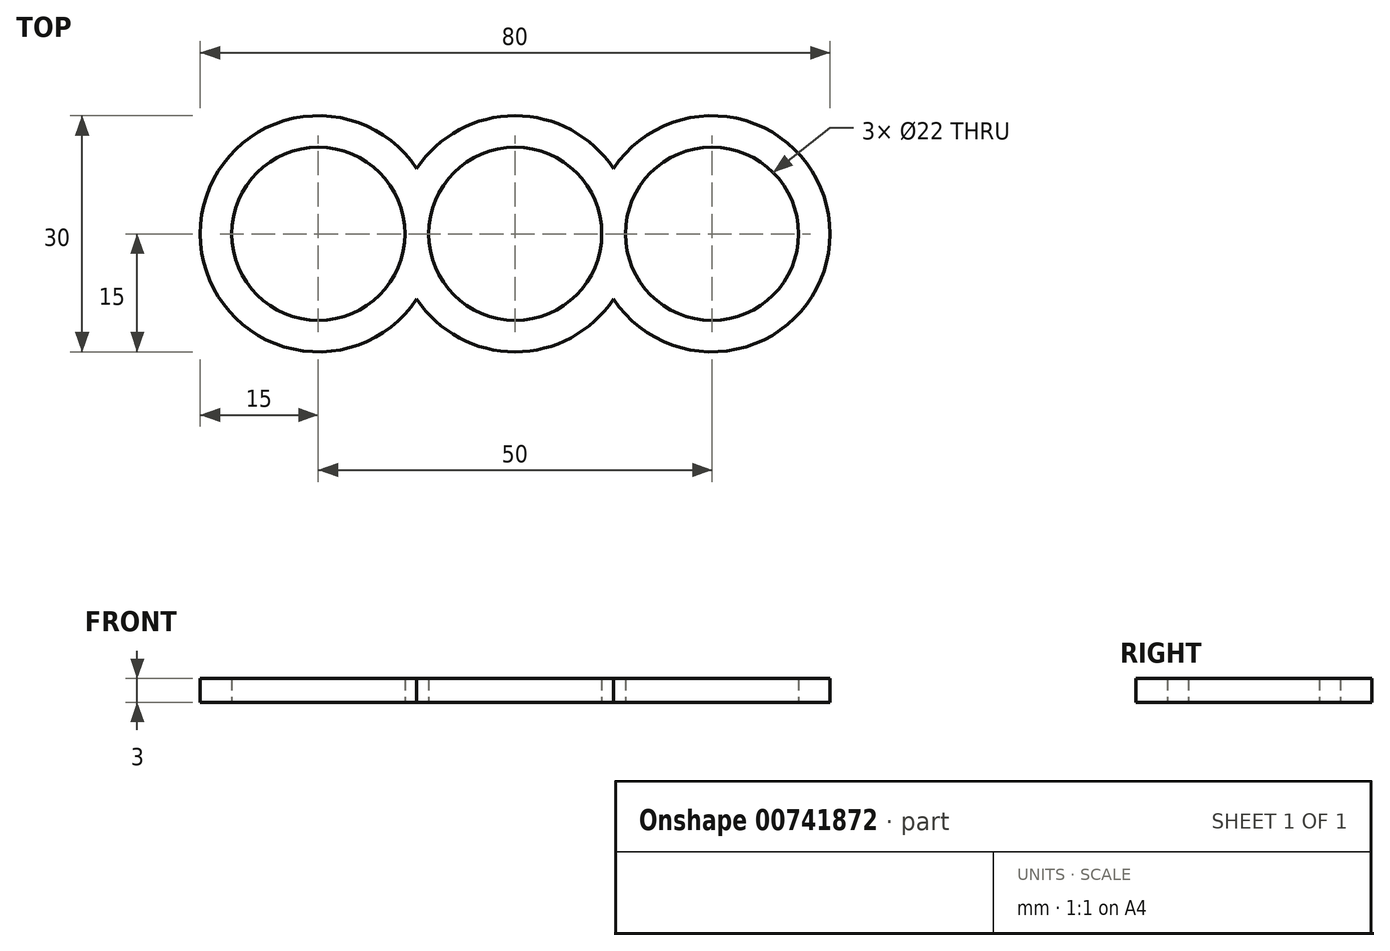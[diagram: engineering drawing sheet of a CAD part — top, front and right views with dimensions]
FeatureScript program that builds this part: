
annotation { "Feature Type Name" : "Feature", "Feature Type Description" : "" }
export const myFeature = defineFeature(function(context is Context, id is Id, definition is map)
    precondition{}
    {
        {
            var Q0;
            Q0=qCreatedBy(makeId("Top.planeOp"),FACE);
            var sketch = newSketch(context, id + "F0", { "sketchPlane" : qUnion([Q0])});
            skArc(sketch, "E0", {"start": v(-12.5, -8.3) * mm, "mid": v(-7.1, -13.22) * mm, "end": v(0, -15) * mm});
            skArc(sketch, "E1", {"start": v(0, 11) * mm, "mid": v(-11, 0) * mm, "end": v(0, -11) * mm});
            skCircle(sketch, "E2", {"center": v(-25, 0) * mm, "radius": 11 * mm});
            skArc(sketch, "E3", {"start": v(-12.5, 8.3) * mm, "mid": v(-40, 0) * mm, "end": v(-12.5, -8.3) * mm});
            skArc(sketch, "E4.trimOffspring", {"start": v(0, 15) * mm, "mid": v(-7.1, 13.22) * mm, "end": v(-12.5, 8.3) * mm});
            skArc(sketch, "E5.MirrorCS", {"start": v(12.5, -8.3) * mm, "mid": v(7.1, -13.22) * mm, "end": v(0, -15) * mm});
            skArc(sketch, "E6.MirrorCS", {"start": v(0, 11) * mm, "mid": v(11, 0) * mm, "end": v(0, -11) * mm});
            skArc(sketch, "E7.MirrorCS", {"start": v(12.5, 8.3) * mm, "mid": v(40, 0) * mm, "end": v(12.5, -8.3) * mm});
            skArc(sketch, "E8.MirrorCS", {"start": v(0, 15) * mm, "mid": v(7.1, 13.22) * mm, "end": v(12.5, 8.3) * mm});
            skCircle(sketch, "E9.MirrorC", {"center": v(25, 0) * mm, "radius": 11 * mm});
            skSolve(sketch);
        }
        {
            var Q0;
            Q0 = qSketchRegion(id + "F0", true);
            extrude(context, id + "F1", {"entities" : qUnion([Q0]), "depth" : 3 * mm, "offsetDistance" : 25 * mm});
        }
    });
